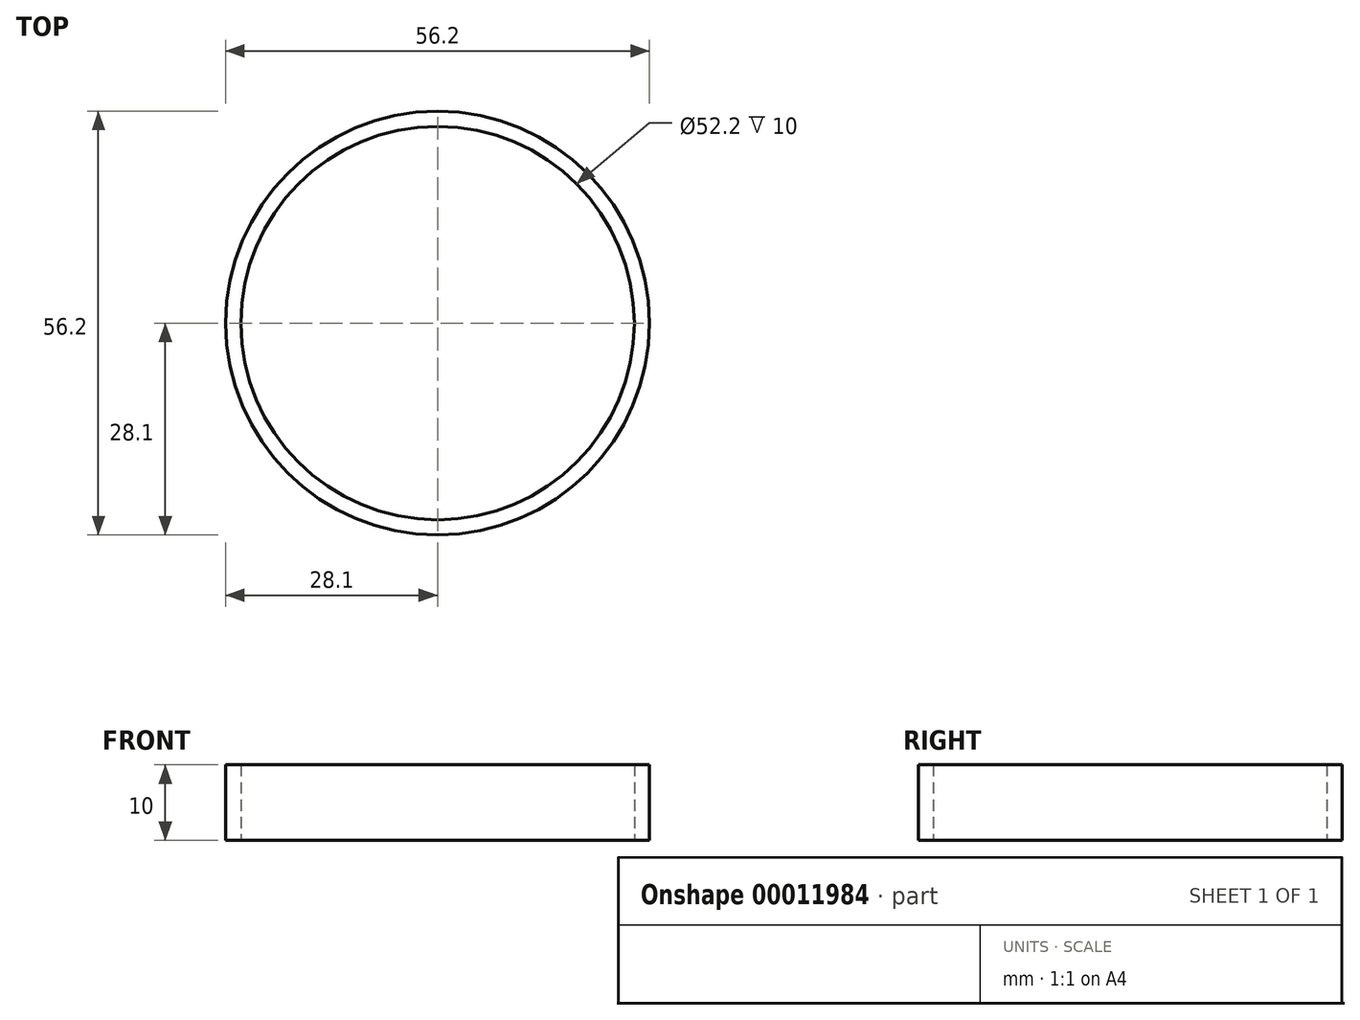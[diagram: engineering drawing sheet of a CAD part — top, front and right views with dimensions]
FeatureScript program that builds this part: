
annotation { "Feature Type Name" : "Feature", "Feature Type Description" : "" }
export const myFeature = defineFeature(function(context is Context, id is Id, definition is map)
    precondition{}
    {
        {
            var Q0;
            Q0=qCreatedBy(makeId("Front.planeOp"),FACE);
            var sketch = newSketch(context, id + "F0", { "sketchPlane" : qUnion([Q0])});
            skLineSegment(sketch, "E0", {"start": v(0, 0) * mm, "end": v(0, 92.85) * mm});
            skLineSegment(sketch, "E1.0", {"start": v(-26.1, 0) * mm, "end": v(-26.1, 10) * mm});
            skLineSegment(sketch, "E2", {"start": v(-26.1, 0) * mm, "end": v(-28.1, 0) * mm});
            skLineSegment(sketch, "E3.0", {"start": v(-26.1, 10) * mm, "end": v(-28.1, 10) * mm});
            skLineSegment(sketch, "E4.0", {"start": v(-28.1, 0) * mm, "end": v(-28.1, 10) * mm});
            skEllipticalArc(sketch, "E5", {});
            skArc(sketch, "E6", {"start": v(-51.85, 60) * mm, "mid": v(-55.43, 58.54) * mm, "end": v(-56.98, 55) * mm});
            skPoint(sketch, "E7.start.orphan", {"position": v(-39.94, 60) * mm});
            skPoint(sketch, "E8.first.point", {"position": v(-52, 59.38) * mm});
            skPoint(sketch, "E8.second.point", {"position": v(-52, 50.61) * mm});
            skPoint(sketch, "E8.third.point", {"position": v(-47.54, 55.59) * mm});
            skLineSegment(sketch, "E9.trimOffspring", {"start": v(-52, 55) * mm, "end": v(-52, 54.74) * mm});
            skFitSpline(sketch, "E10.0", {"points": [v(-50.38, 61.95) * mm, v(-51.85, 62.02) * mm, v(-53.32, 61.95) * mm, v(-55.26, 61.67) * mm, v(-57.64, 60.98) * mm, v(-60.38, 59.64) * mm, v(-62.98, 57.82) * mm, v(-65.44, 55.57) * mm, v(-67.74, 52.89) * mm, v(-69.53, 50.32) * mm, v(-70.88, 48.07) * mm, v(-71.84, 46.28) * mm, v(-72.76, 44.41) * mm, v(-73.9, 41.83) * mm, v(-75.2, 38.43) * mm, v(-76.53, 34.1) * mm, v(-77.63, 29.58) * mm, v(-78.5, 24.87) * mm, v(-79.13, 20.02) * mm, v(-79.45, 15.88) * mm, v(-79.58, 12.53) * mm, v(-79.6, 10) * mm, v(-79.58, 7.46) * mm, v(-79.45, 4.11) * mm, v(-79.13, -0.03) * mm, v(-78.5, -4.88) * mm, v(-77.63, -9.58) * mm, v(-76.53, -14.11) * mm, v(-75.2, -18.43) * mm, v(-73.9, -21.83) * mm, v(-72.76, -24.42) * mm, v(-71.84, -26.29) * mm, v(-70.88, -28.07) * mm, v(-69.53, -30.32) * mm, v(-67.74, -32.9) * mm, v(-65.44, -35.57) * mm, v(-62.98, -37.83) * mm, v(-60.38, -39.64) * mm, v(-57.64, -40.98) * mm, v(-55.26, -41.67) * mm, v(-53.32, -41.95) * mm, v(-51.85, -42.03) * mm, v(-50.38, -41.95) * mm, v(-48.44, -41.67) * mm, v(-46.06, -40.98) * mm, v(-43.32, -39.64) * mm, v(-40.72, -37.83) * mm, v(-38.26, -35.57) * mm, v(-35.95, -32.9) * mm, v(-34.17, -30.32) * mm, v(-32.82, -28.07) * mm, v(-31.86, -26.29) * mm, v(-30.94, -24.42) * mm, v(-29.8, -21.83) * mm, v(-28.5, -18.43) * mm, v(-27.17, -14.11) * mm, v(-26.07, -9.58) * mm, v(-25.2, -4.88) * mm, v(-24.57, -0.03) * mm, v(-24.25, 4.11) * mm, v(-24.12, 7.46) * mm, v(-24.09, 10) * mm, v(-24.12, 12.53) * mm, v(-24.25, 15.88) * mm, v(-24.57, 20.02) * mm, v(-25.2, 24.87) * mm, v(-26.07, 29.58) * mm, v(-27.17, 34.1) * mm, v(-28.5, 38.43) * mm, v(-29.8, 41.83) * mm, v(-30.94, 44.41) * mm, v(-31.86, 46.28) * mm, v(-32.82, 48.07) * mm, v(-34.17, 50.32) * mm, v(-35.95, 52.89) * mm, v(-38.26, 55.57) * mm, v(-40.72, 57.82) * mm, v(-43.32, 59.64) * mm, v(-46.06, 60.98) * mm, v(-48.44, 61.67) * mm, v(-50.38, 61.95) * mm, v(-51.85, 62.02) * mm, v(-53.32, 61.95) * mm]});
            skArc(sketch, "E11", {"start": v(-51.85, 62) * mm, "mid": v(-56.5, 59.89) * mm, "end": v(-57.96, 55) * mm});
            skLineSegment(sketch, "E12", {"start": v(-51.85, 49.73) * mm, "end": v(-51.85, 49.65) * mm});
            skArc(sketch, "E13", {"start": v(-28.1, 10) * mm, "mid": v(-26.92, 11.07) * mm, "end": v(-26.13, 12.46) * mm});
            skLineSegment(sketch, "E14", {"start": v(-24.1, 10) * mm, "end": v(-26.1, 10) * mm});
            skPoint(sketch, "E15.orphan", {"position": v(-28.02, 60) * mm});
            skLineSegment(sketch, "E16", {"start": v(-56.98, 55) * mm, "end": v(-57.96, 55) * mm});
            const initialGuessF0  = {"E5": [-0.051849066753633696, 0.009998090540749897, 0, 1, 0.05, 0.025749066772031117, 4.761548988572434, 0]};
            skSetInitialGuess(sketch, initialGuessF0);
            skSolve(sketch);
        }
        {
            var Q0;
            Q0 = qSketchRegion(id + "F0", true);
            var Q1;
            Q1=sQuery(id+"F0.wireOp",EDGE,"E0");
            revolve(context, id + "F1", {"entities" : qUnion([Q0]), "axis" : qUnion([Q1]), "revolveType" : RevolveType.FULL});
        }
        {
            var Q0;
            Q0 = qSketchRegion(id + "F0", true);
            var Q1;
            Q1=sQuery(id+"F0.wireOp",EDGE,"E0");
            revolve(context, id + "F2", {"operationType" : NewBodyOperationType.ADD, "entities" : qUnion([Q0]), "axis" : qUnion([Q1]), "revolveType" : RevolveType.FULL});
        }
    });
